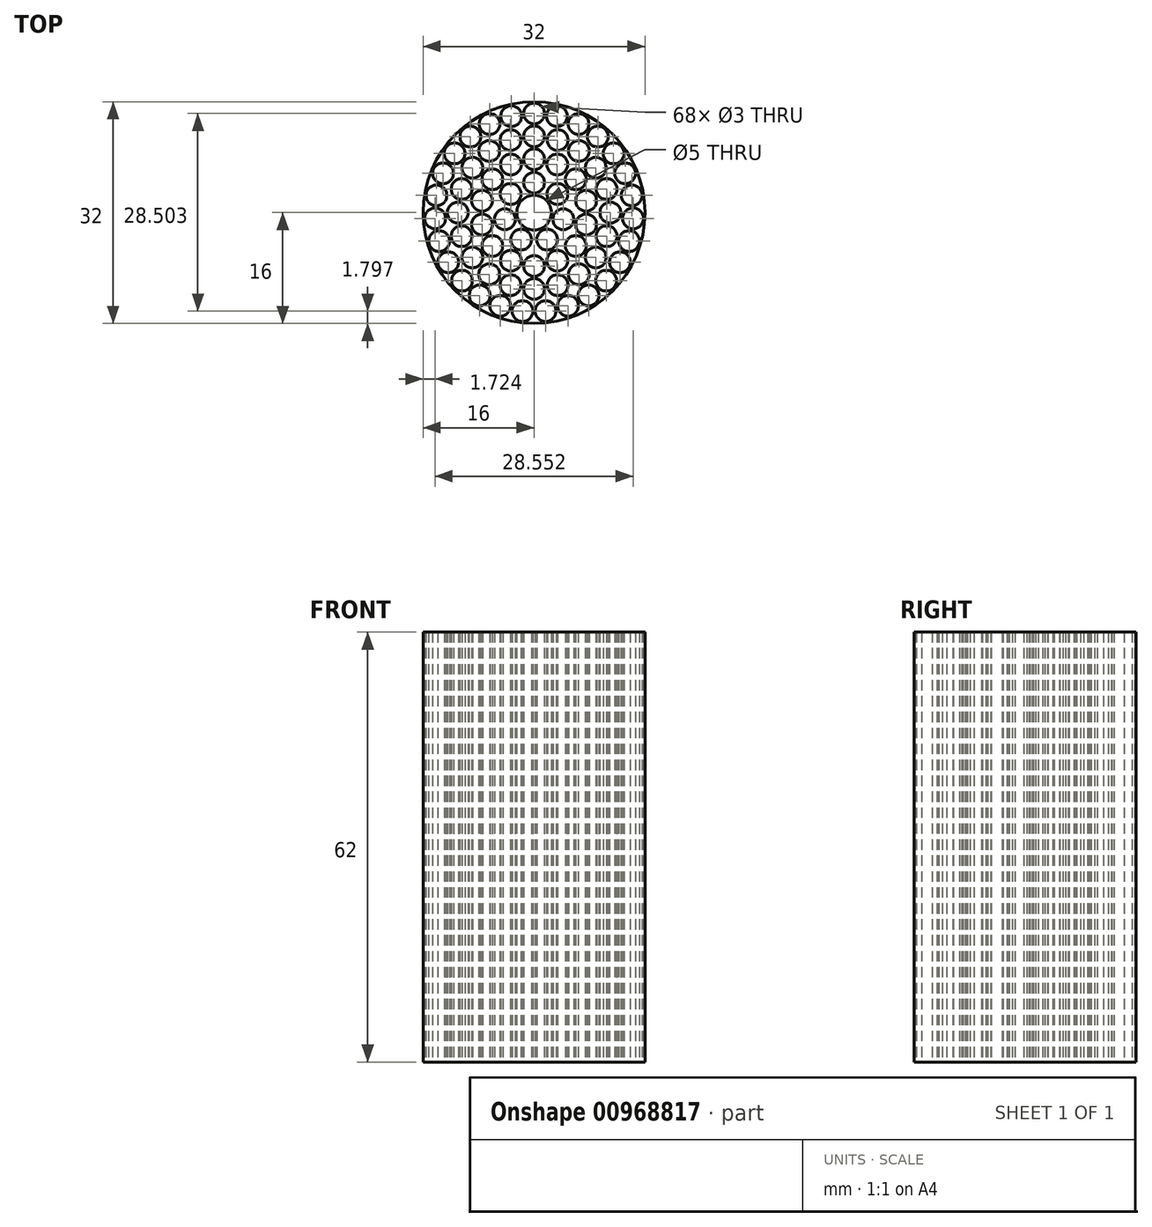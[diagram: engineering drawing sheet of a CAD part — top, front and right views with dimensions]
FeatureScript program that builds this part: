
annotation { "Feature Type Name" : "Feature", "Feature Type Description" : "" }
export const myFeature = defineFeature(function(context is Context, id is Id, definition is map)
    precondition{}
    {
        {
            var Q0;
            Q0=qCreatedBy(makeId("Top.planeOp"),FACE);
            var sketch = newSketch(context, id + "F0", { "sketchPlane" : qUnion([Q0])});
            skCircle(sketch, "E0", {"center": v(0, 0) * mm, "radius": 16 * mm});
            skCircle(sketch, "E1", {"center": v(0, 14.3) * mm, "radius": 1.5 * mm});
            skCircle(sketch, "E2.1.0", {"center": v(-3.3, 13.91) * mm, "radius": 1.5 * mm});
            skCircle(sketch, "E2.2.0", {"center": v(-6.42, 12.78) * mm, "radius": 1.5 * mm});
            skCircle(sketch, "E2.3.0", {"center": v(-9.2, 10.95) * mm, "radius": 1.5 * mm});
            skCircle(sketch, "E2.4.0", {"center": v(-11.47, 8.54) * mm, "radius": 1.5 * mm});
            skCircle(sketch, "E2.5.0", {"center": v(-13.13, 5.66) * mm, "radius": 1.5 * mm});
            skCircle(sketch, "E2.6.0", {"center": v(-14.08, 2.48) * mm, "radius": 1.5 * mm});
            skCircle(sketch, "E2.7.0", {"center": v(-14.28, -0.83) * mm, "radius": 1.5 * mm});
            skCircle(sketch, "E2.8.0", {"center": v(-13.7, -4.1) * mm, "radius": 1.5 * mm});
            skCircle(sketch, "E2.9.0", {"center": v(-12.38, -7.15) * mm, "radius": 1.5 * mm});
            skCircle(sketch, "E2.10.0", {"center": v(-10.4, -9.81) * mm, "radius": 1.5 * mm});
            skCircle(sketch, "E2.11.0", {"center": v(-7.86, -11.95) * mm, "radius": 1.5 * mm});
            skCircle(sketch, "E2.12.0", {"center": v(-4.9, -13.44) * mm, "radius": 1.5 * mm});
            skCircle(sketch, "E2.13.0", {"center": v(-1.66, -14.2) * mm, "radius": 1.5 * mm});
            skCircle(sketch, "E2.14.0", {"center": v(1.66, -14.2) * mm, "radius": 1.5 * mm});
            skCircle(sketch, "E2.15.0", {"center": v(4.9, -13.44) * mm, "radius": 1.5 * mm});
            skCircle(sketch, "E2.16.0", {"center": v(7.86, -11.95) * mm, "radius": 1.5 * mm});
            skCircle(sketch, "E2.17.0", {"center": v(10.4, -9.81) * mm, "radius": 1.5 * mm});
            skCircle(sketch, "E2.18.0", {"center": v(12.38, -7.15) * mm, "radius": 1.5 * mm});
            skCircle(sketch, "E2.19.0", {"center": v(13.7, -4.1) * mm, "radius": 1.5 * mm});
            skCircle(sketch, "E2.20.0", {"center": v(14.28, -0.83) * mm, "radius": 1.5 * mm});
            skCircle(sketch, "E2.21.0", {"center": v(14.08, 2.48) * mm, "radius": 1.5 * mm});
            skCircle(sketch, "E2.22.0", {"center": v(13.13, 5.66) * mm, "radius": 1.5 * mm});
            skCircle(sketch, "E2.23.0", {"center": v(11.47, 8.54) * mm, "radius": 1.5 * mm});
            skCircle(sketch, "E2.24.0", {"center": v(9.2, 10.95) * mm, "radius": 1.5 * mm});
            skCircle(sketch, "E2.25.0", {"center": v(6.42, 12.78) * mm, "radius": 1.5 * mm});
            skCircle(sketch, "E2.26.0", {"center": v(3.3, 13.91) * mm, "radius": 1.5 * mm});
            skCircle(sketch, "E3", {"center": v(0, 11) * mm, "radius": 1.5 * mm});
            skCircle(sketch, "E4.1.0", {"center": v(-3.4, 10.46) * mm, "radius": 1.5 * mm});
            skCircle(sketch, "E4.2.0", {"center": v(-6.47, 8.9) * mm, "radius": 1.5 * mm});
            skCircle(sketch, "E4.3.0", {"center": v(-8.9, 6.47) * mm, "radius": 1.5 * mm});
            skCircle(sketch, "E4.4.0", {"center": v(-10.46, 3.4) * mm, "radius": 1.5 * mm});
            skCircle(sketch, "E4.5.0", {"center": v(-11, 0) * mm, "radius": 1.5 * mm});
            skCircle(sketch, "E4.6.0", {"center": v(-10.46, -3.4) * mm, "radius": 1.5 * mm});
            skCircle(sketch, "E4.7.0", {"center": v(-8.9, -6.47) * mm, "radius": 1.5 * mm});
            skCircle(sketch, "E4.8.0", {"center": v(-6.47, -8.9) * mm, "radius": 1.5 * mm});
            skCircle(sketch, "E4.9.0", {"center": v(-3.4, -10.46) * mm, "radius": 1.5 * mm});
            skCircle(sketch, "E4.10.0", {"center": v(0, -11) * mm, "radius": 1.5 * mm});
            skCircle(sketch, "E4.11.0", {"center": v(3.4, -10.46) * mm, "radius": 1.5 * mm});
            skCircle(sketch, "E4.12.0", {"center": v(6.47, -8.9) * mm, "radius": 1.5 * mm});
            skCircle(sketch, "E4.13.0", {"center": v(8.9, -6.47) * mm, "radius": 1.5 * mm});
            skCircle(sketch, "E4.14.0", {"center": v(10.46, -3.4) * mm, "radius": 1.5 * mm});
            skCircle(sketch, "E4.15.0", {"center": v(11, 0) * mm, "radius": 1.5 * mm});
            skCircle(sketch, "E4.16.0", {"center": v(10.46, 3.4) * mm, "radius": 1.5 * mm});
            skCircle(sketch, "E4.17.0", {"center": v(8.9, 6.47) * mm, "radius": 1.5 * mm});
            skCircle(sketch, "E4.18.0", {"center": v(6.47, 8.9) * mm, "radius": 1.5 * mm});
            skCircle(sketch, "E4.19.0", {"center": v(3.4, 10.46) * mm, "radius": 1.5 * mm});
            skCircle(sketch, "E5", {"center": v(0, 7.7) * mm, "radius": 1.5 * mm});
            skCircle(sketch, "E6.1.0", {"center": v(-3.34, 6.94) * mm, "radius": 1.5 * mm});
            skCircle(sketch, "E6.2.0", {"center": v(-6.02, 4.8) * mm, "radius": 1.5 * mm});
            skCircle(sketch, "E6.3.0", {"center": v(-7.5, 1.71) * mm, "radius": 1.5 * mm});
            skCircle(sketch, "E6.4.0", {"center": v(-7.5, -1.71) * mm, "radius": 1.5 * mm});
            skCircle(sketch, "E6.5.0", {"center": v(-6.02, -4.8) * mm, "radius": 1.5 * mm});
            skCircle(sketch, "E6.6.0", {"center": v(-3.34, -6.94) * mm, "radius": 1.5 * mm});
            skCircle(sketch, "E6.7.0", {"center": v(0, -7.7) * mm, "radius": 1.5 * mm});
            skCircle(sketch, "E6.8.0", {"center": v(3.34, -6.94) * mm, "radius": 1.5 * mm});
            skCircle(sketch, "E6.9.0", {"center": v(6.02, -4.8) * mm, "radius": 1.5 * mm});
            skCircle(sketch, "E6.10.0", {"center": v(7.5, -1.71) * mm, "radius": 1.5 * mm});
            skCircle(sketch, "E6.11.0", {"center": v(7.5, 1.71) * mm, "radius": 1.5 * mm});
            skCircle(sketch, "E6.12.0", {"center": v(6.02, 4.8) * mm, "radius": 1.5 * mm});
            skCircle(sketch, "E6.13.0", {"center": v(3.34, 6.94) * mm, "radius": 1.5 * mm});
            skCircle(sketch, "E7", {"center": v(0, 4.32) * mm, "radius": 1.5 * mm});
            skCircle(sketch, "E8.1.0", {"center": v(-3.38, 2.7) * mm, "radius": 1.5 * mm});
            skCircle(sketch, "E8.2.0", {"center": v(-4.21, -0.96) * mm, "radius": 1.5 * mm});
            skCircle(sketch, "E8.3.0", {"center": v(-1.87, -3.9) * mm, "radius": 1.5 * mm});
            skCircle(sketch, "E8.4.0", {"center": v(1.87, -3.9) * mm, "radius": 1.5 * mm});
            skCircle(sketch, "E8.5.0", {"center": v(4.21, -0.96) * mm, "radius": 1.5 * mm});
            skCircle(sketch, "E8.6.0", {"center": v(3.38, 2.7) * mm, "radius": 1.5 * mm});
            skCircle(sketch, "E9", {"center": v(0, 0) * mm, "radius": 2.5 * mm});
            skSolve(sketch);
        }
        {
            var Q0;
            Q0=makeQuery(id+"F0.imprint","IMPRINT",FACE,{"disambiguationData":[TD([[makeQuery(id+"F0.imprint","IMPRINT",EDGE,{"derivedFrom":sQuery(id+"F0.wireOp",EDGE,"E0")}),1.0]])]});
            extrude(context, id + "F1", {"entities" : qUnion([Q0]), "depth" : 62 * mm, "offsetDistance" : 25 * mm});
        }
    });
